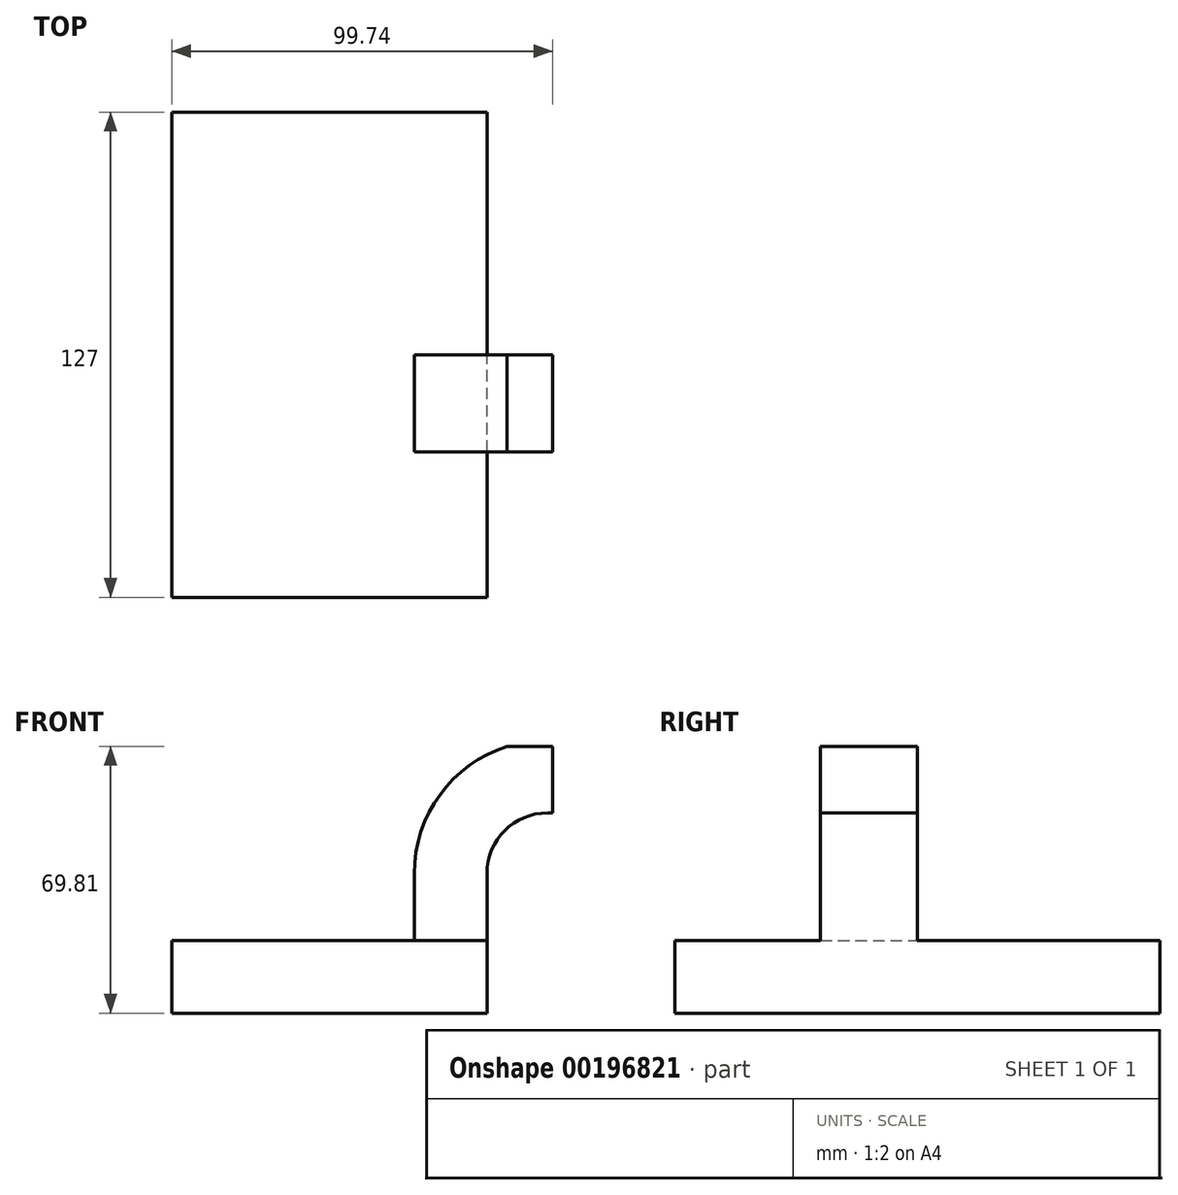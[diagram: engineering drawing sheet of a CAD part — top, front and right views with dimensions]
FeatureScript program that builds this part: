
annotation { "Feature Type Name" : "Feature", "Feature Type Description" : "" }
export const myFeature = defineFeature(function(context is Context, id is Id, definition is map)
    precondition{}
    {
        {
            var Q0;
            Q0=qCreatedBy(makeId("Front.planeOp"),FACE);
            var sketch = newSketch(context, id + "F0", { "sketchPlane" : qUnion([Q0])});
            skLineSegment(sketch, "E0.bottom", {"start": v(41.28, -9.52) * mm, "end": v(-41.28, -9.53) * mm});
            skLineSegment(sketch, "E0.top", {"start": v(41.28, 9.53) * mm, "end": v(-41.28, 9.52) * mm});
            skLineSegment(sketch, "E0.left", {"start": v(41.28, -9.52) * mm, "end": v(41.28, 9.53) * mm});
            skLineSegment(sketch, "E0.right", {"start": v(-41.28, -9.53) * mm, "end": v(-41.28, 9.52) * mm});
            skPoint(sketch, "E0.middle", {"position": v(0, 0) * mm});
            skLineSegment(sketch, "E1.bottom", {"start": v(109.26, 38.1) * mm, "end": v(58.46, 38.1) * mm});
            skLineSegment(sketch, "E1.top", {"start": v(109.26, 66.68) * mm, "end": v(58.46, 66.68) * mm});
            skLineSegment(sketch, "E1.left", {"start": v(109.26, 38.1) * mm, "end": v(109.26, 66.68) * mm});
            skLineSegment(sketch, "E1.right", {"start": v(58.46, 38.1) * mm, "end": v(58.46, 66.68) * mm});
            skPoint(sketch, "E1.middle", {"position": v(83.86, 52.39) * mm});
            skLineSegment(sketch, "E2", {"start": v(41.28, 9.53) * mm, "end": v(41.28, 27) * mm});
            skArc(sketch, "E3", {"start": v(41.28, 27) * mm, "mid": v(45.92, 38.23) * mm, "end": v(57.15, 42.88) * mm});
            skLineSegment(sketch, "E4", {"start": v(57.15, 42.88) * mm, "end": v(89.34, 42.88) * mm});
            skArc(sketch, "E5.0", {"start": v(22.23, 27) * mm, "mid": v(28.95, 47.6) * mm, "end": v(46.55, 60.28) * mm});
            skLineSegment(sketch, "E5.1", {"start": v(22.23, 9.53) * mm, "end": v(22.23, 27) * mm});
            skLineSegment(sketch, "E6", {"start": v(46.55, 60.28) * mm, "end": v(78.73, 60.28) * mm});
            skFitSpline(sketch, "E7", {"points": [v(-41.28, 9.52) * mm, v(46.55, 60.28) * mm], "startDerivative": vector(35.08, 104.43) * mm, "endDerivative": vector(113.05, 14.14) * mm});
            skSolve(sketch);
        }
        {
            var Q0;
            Q0=makeQuery(id+"F0.imprint","IMPRINT",FACE,{"disambiguationData":[TD([[makeQuery(id+"F0.imprint","IMPRINT",EDGE,{"derivedFrom":sQuery(id+"F0.wireOp",EDGE,"E0.bottom")}),-1.0]])]});
            extrude(context, id + "F1", {"entities" : qUnion([Q0]), "endBound" : BoundingType.SYMMETRIC, "depth" : 127 * mm});
        }
        {
            var Q0;
            {var subQ5=sQuery(id+"F0.wireOp",EDGE,"E2");Q0=makeQuery(id+"F0.imprint","IMPRINT",FACE,{"disambiguationData":[TD([[makeQuery(id+"F0.imprint","IMPRINT",EDGE,{"derivedFrom":subQ5}),1.0]])]});}
            var Q1;
            Q1=makeQuery(id+"F0.imprint","IMPRINT",FACE,{"disambiguationData":[TD([[makeQuery(id+"F0.imprint","IMPRINT",EDGE,{"derivedFrom":sQuery(id+"F0.wireOp",EDGE,"E5.0")}),1.0]])]});
            extrude(context, id + "F2", {"entities" : qUnion([Q0, Q1]), "operationType" : NewBodyOperationType.ADD, "depth" : 25.4 * mm});
        }
    });
